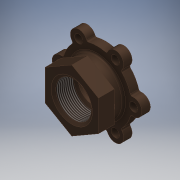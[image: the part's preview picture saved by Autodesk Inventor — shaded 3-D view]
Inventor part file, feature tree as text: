
AUTODESK INVENTOR PART (.ipt)
format: ipt  version: 2018 (Build 220112000, 112)  size: 293,888 bytes
history: native  units: mm
features: sketch x3, extrude x3, revolve x1, thread x1, fillet x1
ambient origin geometry x8: Origin, YZ Plane, XZ Plane, XY Plane, X Axis, Y Axis, Z Axis, Center Point
bodies: Solid1 (feature_tree)
feature tree (9):
  revolve  "Revolution1"  [1 undecoded]
  thread  "Thread1"  [1 undecoded]
  sketch  "Sketch2"  dims[d6=2.0mm d7=21.0mm]
  extrude  "Extrusion1"  Depth=2.0mm
  sketch  "Sketch3"  dims[d8=26.0mm d9=23.0mm d10=40.0mm d12=29.0mm d13=51.0mm d14=57.0mm d15=5.0mm d16=27.0mm d17=33.0mm d18=36.0mm d19=39.0mm d20=74.0mm d22=32.0mm d23=90.0deg d24=57.0mm d25=10.0mm d26=0.0mm d27=17.0mm d28=0.0mm d29=60.0deg d30=78.0mm d31=9.0mm d32=18.0mm d33=67.0mm d35=60.0mm d37=360.0deg d40=74.0mm d42=9.0mm d43=0.0mm d44=9.0mm d45=0.0mm d46=2.0mm]
  extrude  "Extrusion2"  Depth=2.0mm
  extrude  "Extrusion3"  Depth=2.0mm
  fillet  "Fillet1"  Radius=29.0mm
  sketch  "Sketch1"  dims[d2=38.0mm d3=57.0mm d4=3.0mm]
note: 2 required parameter values undecoded (feature->parameter linkage not recoverable at this tier; creation-order binding heuristic only, values carry confidence <= 0.55)